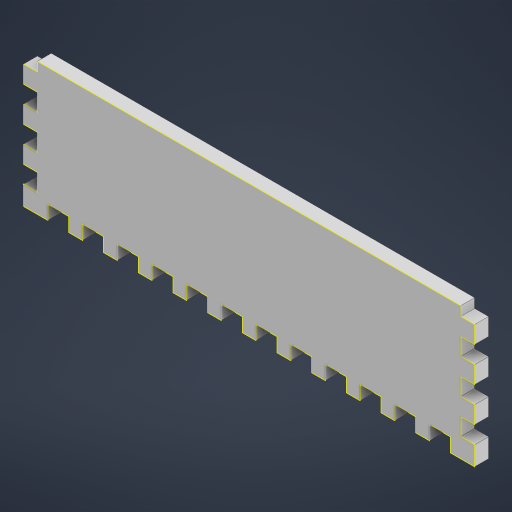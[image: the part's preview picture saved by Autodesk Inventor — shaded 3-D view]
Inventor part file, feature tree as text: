
AUTODESK INVENTOR PART (.ipt)
format: ipt  version: 2023 (Build 270158030, 158C)  size: 297,984 bytes
history: native  units: mm
features: sketch x2, extrude x1, projected_geometry x1
ambient origin geometry x8: Origin, YZ Plane, XZ Plane, XY Plane, X Axis, Y Axis, Z Axis, Center Point
bodies: Solid1 (feature_tree)
feature tree (4):
  extrude  "Extrusion1"  [1 undecoded]
  sketch  "Sketch2"
  sketch  "Sketch1"  dims[d0=4.0mm d1=0.0mm]
  projected_geometry  "Projected Loop1"
note: 1 required parameter value undecoded (feature->parameter linkage not recoverable at this tier; creation-order binding heuristic only, values carry confidence <= 0.55)
